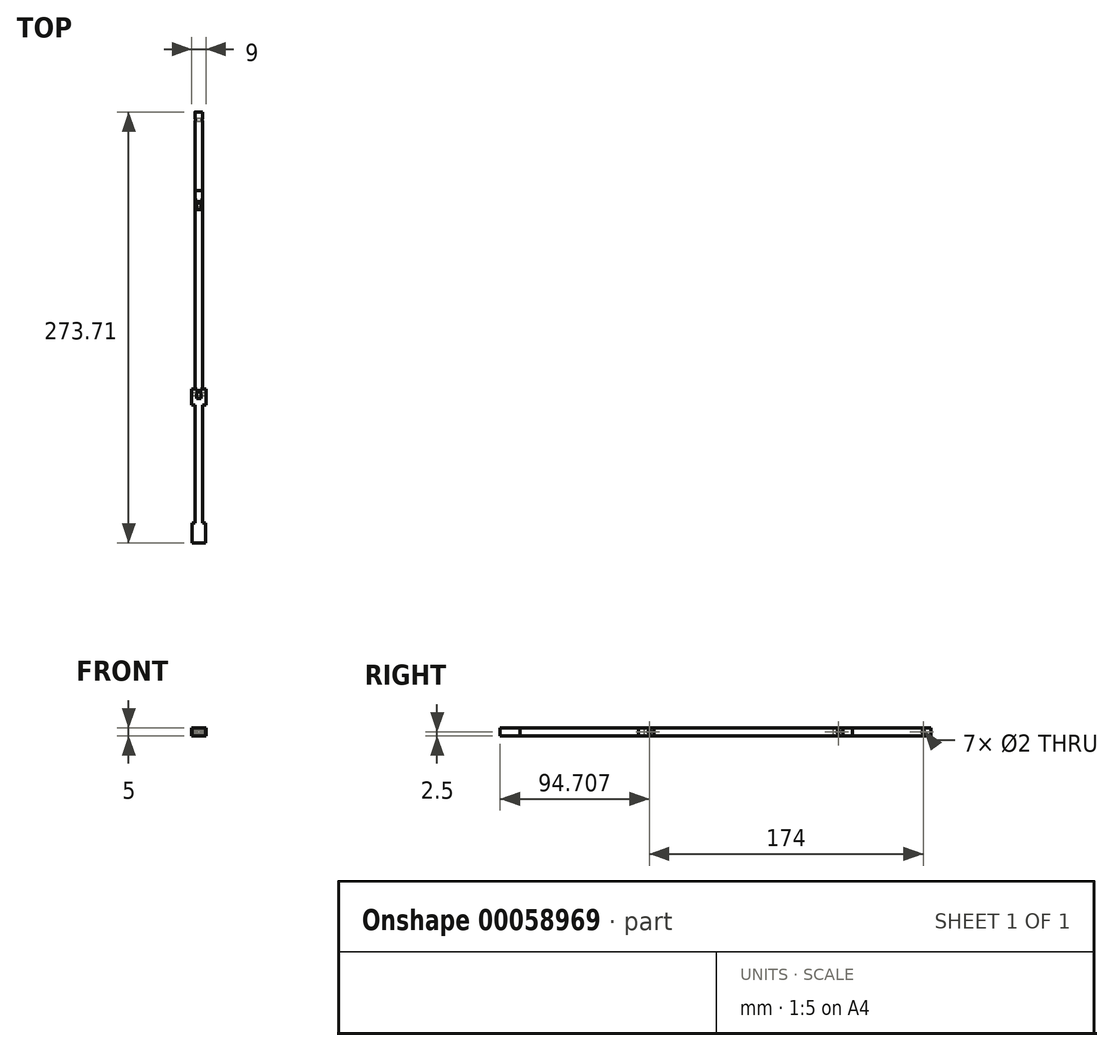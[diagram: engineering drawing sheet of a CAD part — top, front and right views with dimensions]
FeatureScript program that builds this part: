
annotation { "Feature Type Name" : "Feature", "Feature Type Description" : "" }
export const myFeature = defineFeature(function(context is Context, id is Id, definition is map)
    precondition{}
    {
        {
            var Q0;
            Q0=qCreatedBy(makeId("Top.planeOp"),FACE);
            var sketch = newSketch(context, id + "F0", { "sketchPlane" : qUnion([Q0])});
            skLineSegment(sketch, "E0.top", {"start": v(2.38, 39.03) * mm, "end": v(-6.5, 39.03) * mm});
            skLineSegment(sketch, "E0.left", {"start": v(2.38, 26.32) * mm, "end": v(2.38, 39.03) * mm});
            skLineSegment(sketch, "E0.right", {"start": v(-6.5, 26.32) * mm, "end": v(-6.5, 39.03) * mm});
            skLineSegment(sketch, "E1", {"start": v(-6.5, 26.32) * mm, "end": v(2.38, 26.32) * mm});
            skSolve(sketch);
        }
        {
            var Q0;
            Q0=qSketchRegion(id+"F0",true);
            extrude(context, id + "F1", {"entities" : qUnion([Q0]), "depth" : 5 * mm});
        }
        {
            var Q0;
            Q0=makeQuery(id+"F1.opExtrude","SWEPT_FACE",FACE,{"disambiguationData":[OSD([sQuery(id+"F0.wireOp",EDGE,"E0.top")])]});
            var sketch = newSketch(context, id + "F2", { "sketchPlane" : qUnion([Q0])});
            skLineSegment(sketch, "E2.bottom", {"start": v(-2.38, 5) * mm, "end": v(6.5, 5) * mm, "construction": true});
            skLineSegment(sketch, "E2.top", {"start": v(-2.38, 0) * mm, "end": v(6.5, 0) * mm, "construction": true});
            skLineSegment(sketch, "E2.left", {"start": v(-2.38, 5) * mm, "end": v(-2.38, 0) * mm, "construction": true});
            skLineSegment(sketch, "E2.right", {"start": v(6.5, 5) * mm, "end": v(6.5, 0) * mm, "construction": true});
            skLineSegment(sketch, "E3", {"start": v(2.06, 5) * mm, "end": v(2.06, 0) * mm, "construction": true});
            skPoint(sketch, "E4", {"position": v(2.06, 2.5) * mm});
            skLineSegment(sketch, "E5.bottom", {"start": v(-0.44, 5) * mm, "end": v(4.56, 5) * mm});
            skLineSegment(sketch, "E5.top", {"start": v(-0.44, 0) * mm, "end": v(4.56, 0) * mm});
            skLineSegment(sketch, "E5.left", {"start": v(-0.44, 5) * mm, "end": v(-0.44, 0) * mm});
            skLineSegment(sketch, "E5.right", {"start": v(4.56, 5) * mm, "end": v(4.56, 0) * mm});
            skPoint(sketch, "E6", {"position": v(2.06, 5) * mm});
            skSolve(sketch);
        }
        {
            var Q0;
            Q0=makeQuery(id+"F2.imprint","IMPRINT",FACE,{"disambiguationData":[TD([[makeQuery(id+"F2.imprint","IMPRINT",EDGE,{"derivedFrom":sQuery(id+"F2.wireOp",EDGE,"E5.bottom")}),-1.0]])]});
            extrude(context, id + "F3", {"entities" : qUnion([Q0]), "operationType" : NewBodyOperationType.ADD, "depth" : 85 * mm});
        }
        {
            var Q0;
            Q0=makeQuery(id+"F3.boolean.opBoolean","MERGE",FACE,{"derivedFrom":[makeQuery(id+"F1.opExtrude","CAP_FACE",FACE,{"disambiguationData":[OSD([sQuery(id+"F0.wireOp",EDGE,"d9f391bc-674f-497b-be90-560cbfe84b75"),sQuery(id+"F0.wireOp",EDGE,"66b45562-6a73-478d-960d-9298d4f6f7f0"),sQuery(id+"F0.wireOp",EDGE,"14187485-9066-4405-92d3-fc27601e42af"),sQuery(id+"F0.wireOp",EDGE,"531d857a-c366-4fd6-946f-2a201ec59503"),sQuery(id+"F0.wireOp",EDGE,"82b77f9d-e961-41ac-b487-f27284012814"),sQuery(id+"F0.wireOp",EDGE,"7834417a-5e7c-45c5-8e6f-19fbc39ef538"),sQuery(id+"F0.wireOp",EDGE,"300af05a-1d2d-4a39-b159-b80513d7f740"),sQuery(id+"F0.wireOp",EDGE,"1d5f7e8b-d76f-446f-8b3e-2a2f550bd8e3"),sQuery(id+"F0.wireOp",EDGE,"35e8518a-73fa-4b07-8810-64eb534e7b1e"),sQuery(id+"F0.wireOp",EDGE,"18614789-dbbf-47a7-80e0-906205be91d2"),sQuery(id+"F0.wireOp",EDGE,"b77e8b2d-b58d-4b65-9e12-d4334338aa4c"),sQuery(id+"F0.wireOp",EDGE,"9d96ad04-3b06-4638-bbb7-3f0403701198"),sQuery(id+"F0.wireOp",EDGE,"e2f941ec-7ca7-4e10-9b82-3674a8dee568"),sQuery(id+"F0.wireOp",EDGE,"623cfd6c-6096-4034-a234-787e3acb7919"),sQuery(id+"F0.wireOp",EDGE,"effc0b7c-bb45-4b4c-82cf-5a194e7747a9"),sQuery(id+"F0.wireOp",EDGE,"20afc2aa-4987-4b9c-837f-1a90a823d70c"),sQuery(id+"F0.wireOp",EDGE,"93c108a5-420a-46d6-a4f1-9fc166012f6e"),sQuery(id+"F0.wireOp",EDGE,"24f54e41-abe2-49ed-aca4-37dbfc811c90"),sQuery(id+"F0.wireOp",EDGE,"9775e243-409f-4585-bc05-4883512e3564"),sQuery(id+"F0.wireOp",EDGE,"a5e87a16-9f3d-4e96-afb7-1f3010025381"),sQuery(id+"F0.wireOp",EDGE,"57da4376-ad28-41da-a036-1c08f5a0e9fe"),sQuery(id+"F0.wireOp",EDGE,"42ac5c60-1a59-4eb0-a50e-105db2941719"),sQuery(id+"F0.wireOp",EDGE,"7f869c91-c514-4a78-955d-8fa2f71ec013"),sQuery(id+"F0.wireOp",EDGE,"92df5dc1-1633-40e4-82dc-26b14e9fc4fe"),sQuery(id+"F0.wireOp",EDGE,"9fb6344f-8160-4d43-a8ca-7dc5bcb63cf4"),sQuery(id+"F0.wireOp",EDGE,"403433ed-74ab-49ef-b5f3-8321a2a46bc0"),sQuery(id+"F0.wireOp",EDGE,"38791a52-10f3-4032-89cb-9997d4a285ff"),sQuery(id+"F0.wireOp",EDGE,"17827bc5-de02-4b8f-ae35-e25ffe9a3a56"),sQuery(id+"F0.wireOp",EDGE,"ebb8a741-28c9-44e3-8d01-7b9906950363"),sQuery(id+"F0.wireOp",EDGE,"24247562-824f-4080-b562-a07a46203f45"),sQuery(id+"F0.wireOp",EDGE,"61158206-3902-44f4-b84a-59a3b62cea53"),sQuery(id+"F0.wireOp",EDGE,"222b9068-06c2-468c-a816-7dcc0e9861e7"),sQuery(id+"F0.wireOp",EDGE,"1443c47e-cb78-4972-aa1d-b2a5593cacaa"),sQuery(id+"F0.wireOp",EDGE,"4ee5fa2a-e4b7-4507-9879-d4257c452374"),sQuery(id+"F0.wireOp",EDGE,"ac129c3d-c943-4e23-b628-d4f0035e9390"),sQuery(id+"F0.wireOp",EDGE,"a4b60933-6dc5-485c-afad-bad217473213"),sQuery(id+"F0.wireOp",EDGE,"c784899e-bd4b-4296-9021-59274ccaadd9"),sQuery(id+"F0.wireOp",EDGE,"748fc19f-7cd7-4142-921c-8b19d610d3d1"),sQuery(id+"F0.wireOp",EDGE,"ebea3f07-4c38-41c4-ac2c-bac9cb8d1528"),sQuery(id+"F0.wireOp",EDGE,"c6bc3915-ea64-408b-b0c0-442b260292ac"),sQuery(id+"F0.wireOp",EDGE,"15593884-b140-4daf-bfd8-0ecfa5efcbbd"),sQuery(id+"F0.wireOp",EDGE,"a7df4056-7cd6-44bf-9033-605bc9c32d03"),sQuery(id+"F0.wireOp",EDGE,"39d318a8-1c2b-49b4-b444-523ba4d5fcf2"),sQuery(id+"F0.wireOp",EDGE,"11df0492-6635-41a9-8511-0c760388fa34"),sQuery(id+"F0.wireOp",EDGE,"a12d8f92-446a-4b34-a2f5-26c26993d257"),sQuery(id+"F0.wireOp",EDGE,"78a7d225-68f4-4e83-b71e-32c50f125e93"),sQuery(id+"F0.wireOp",EDGE,"1862a963-57d5-471d-8109-9f73d1aa8848"),sQuery(id+"F0.wireOp",EDGE,"54f45445-f8d1-4aff-bece-9da66ad386cd"),sQuery(id+"F0.wireOp",EDGE,"5ba05bdf-983b-4f68-941c-4bf50adfb3c5"),sQuery(id+"F0.wireOp",EDGE,"973eaeb2-d25f-40eb-b74f-e363d637089d"),sQuery(id+"F0.wireOp",EDGE,"9fe65cb9-7a78-4622-86d1-7f23de040810"),sQuery(id+"F0.wireOp",EDGE,"3fe47919-788c-4396-b5fd-8990ec275c22"),sQuery(id+"F0.wireOp",EDGE,"55bf8aa7-cfd1-4645-9e83-de087904feb2"),sQuery(id+"F0.wireOp",EDGE,"c2af9e0f-cc3a-474c-a54e-54ce149af3bb"),sQuery(id+"F0.wireOp",EDGE,"ff518af7-eed7-424f-ad46-c5242196626b"),sQuery(id+"F0.wireOp",EDGE,"cc0332f5-aef5-4de5-a14e-8dcbe21eca6c"),sQuery(id+"F0.wireOp",EDGE,"c5d08f8f-8ed2-45eb-9a75-cb5f251a4d6d"),sQuery(id+"F0.wireOp",EDGE,"5995e242-d37b-4450-9f63-962c7eb38085"),sQuery(id+"F0.wireOp",EDGE,"25f3b115-5ae4-4790-92e5-62a7bc3f5c29"),sQuery(id+"F0.wireOp",EDGE,"2d611a70-a2f5-475a-a6a8-adddd76473ce"),sQuery(id+"F0.wireOp",EDGE,"273bf26d-3f66-4ef4-bf64-d22a533f903a"),sQuery(id+"F0.wireOp",EDGE,"de5f23e0-e1a0-4e15-900e-688ab9168dcd"),sQuery(id+"F0.wireOp",EDGE,"4de6b542-ff3a-44f7-b58e-1e4f3b2cccf4"),sQuery(id+"F0.wireOp",EDGE,"be1b36f0-e020-4af0-baec-c4481b6b9122"),sQuery(id+"F0.wireOp",EDGE,"d7c1d08a-2f0c-4649-94c4-8f89162c768a"),sQuery(id+"F0.wireOp",EDGE,"bd09b6b8-9bc9-4c5b-ab2b-4ede4d9b9cae"),sQuery(id+"F0.wireOp",EDGE,"05b5a1f0-0223-4439-ac6f-cac7d6a05357"),sQuery(id+"F0.wireOp",EDGE,"318e3676-c449-41e0-b4da-e74d07fc2b12"),sQuery(id+"F0.wireOp",EDGE,"31725f89-0695-4483-9200-5756053d80e4"),sQuery(id+"F0.wireOp",EDGE,"e3cb0712-5583-40de-9f57-2bae5fcde790"),sQuery(id+"F0.wireOp",EDGE,"c6456fea-21fc-4931-a427-a856d1f6ee5c"),sQuery(id+"F0.wireOp",EDGE,"e7d8b0b0-a421-4050-b770-ef5136dc3e4d"),sQuery(id+"F0.wireOp",EDGE,"0788d0b0-f754-45d8-aefc-a91755a03ac1"),sQuery(id+"F0.wireOp",EDGE,"fc27efed-591c-43cc-b4b2-6872e1742544"),sQuery(id+"F0.wireOp",EDGE,"82c2f9b8-58bc-4a33-9bd5-fec435af3e72"),sQuery(id+"F0.wireOp",EDGE,"2e300663-fb6b-4f29-9ebf-a9fab34af9c4"),sQuery(id+"F0.wireOp",EDGE,"3d2dfd07-a0b9-43b8-893f-685d0a355372"),sQuery(id+"F0.wireOp",EDGE,"e776ef69-6530-4f3d-8924-f9840dcd9e4d"),sQuery(id+"F0.wireOp",EDGE,"6dcbcc22-e493-4400-9b8a-7eed73031bc4"),sQuery(id+"F0.wireOp",EDGE,"7cdd9895-84d3-47ea-86bd-688608d79eca"),sQuery(id+"F0.wireOp",EDGE,"3a7bfdfd-3144-4dae-8888-a8bcf2221552"),sQuery(id+"F0.wireOp",EDGE,"2953d7e0-23a1-472e-bf8c-49982d9a56d6"),sQuery(id+"F0.wireOp",EDGE,"846718aa-0a8a-476e-8a52-f2d355658347"),sQuery(id+"F0.wireOp",EDGE,"13e02fad-2dbd-4394-a12b-883b621fb0cf"),sQuery(id+"F0.wireOp",EDGE,"9bfc4f6e-5194-4c80-9375-02c13d7037c7"),sQuery(id+"F0.wireOp",EDGE,"4cc90906-b22a-4bfe-9933-4a2b42c67043"),sQuery(id+"F0.wireOp",EDGE,"c3968d64-93bc-4dc6-b8a7-840e206f0e92"),sQuery(id+"F0.wireOp",EDGE,"cff9c3c0-4237-426c-aea8-7115d6da3525"),sQuery(id+"F0.wireOp",EDGE,"76e5b534-b14d-4a45-9111-d87c94f3d3da"),sQuery(id+"F0.wireOp",EDGE,"96eb4b59-6d18-41e9-8181-93777d457c04"),sQuery(id+"F0.wireOp",EDGE,"4b80822d-625d-4929-946d-bb2fee906de1"),sQuery(id+"F0.wireOp",EDGE,"a1b1815c-0f60-4723-aacc-aafe0ccbf065"),sQuery(id+"F0.wireOp",EDGE,"63631a9c-c3d0-4e34-b42e-cf718a2aa654"),sQuery(id+"F0.wireOp",EDGE,"291662e0-8a9a-4794-9b05-15f69232fded"),sQuery(id+"F0.wireOp",EDGE,"c31bbd6a-e51d-4bda-bb55-a930242c1aae"),sQuery(id+"F0.wireOp",EDGE,"6cc65a5c-01cd-414d-b4bf-16365d086d8b"),sQuery(id+"F0.wireOp",EDGE,"0f6044bc-5aed-4332-8dd0-ed4f837cf9c8"),sQuery(id+"F0.wireOp",EDGE,"68f51909-fb33-4c21-8354-d3ee43222832"),sQuery(id+"F0.wireOp",EDGE,"0ba4c335-165f-4c3e-a523-b257962ab2b9"),sQuery(id+"F0.wireOp",EDGE,"a8ab603d-6f8c-4c2b-bc3e-a90f3d25e983"),sQuery(id+"F0.wireOp",EDGE,"3346a9eb-c449-4294-82ff-d0765618b8c3"),sQuery(id+"F0.wireOp",EDGE,"efd91459-38fa-452e-891e-edab332f6489"),sQuery(id+"F0.wireOp",EDGE,"85b94afd-6a00-47ab-a374-eb0a6b957af6"),sQuery(id+"F0.wireOp",EDGE,"71bbe033-8d0c-4649-8752-095e423e4446"),sQuery(id+"F0.wireOp",EDGE,"313f4505-8deb-44f7-a07b-deab9fdd4fca"),sQuery(id+"F0.wireOp",EDGE,"58514e34-5bb3-46cf-af5d-05d66b0c10f9"),sQuery(id+"F0.wireOp",EDGE,"9c61e8f2-2ab1-4688-a9d6-5c20a88d6f6a"),sQuery(id+"F0.wireOp",EDGE,"f84fcc24-327f-4d24-8afc-1352f07d6813"),sQuery(id+"F0.wireOp",EDGE,"2217ef4b-fa2d-4c42-8d86-ed7db710f5bd"),sQuery(id+"F0.wireOp",EDGE,"d87f30a8-b645-4562-81e4-3c3cf9cd6438"),sQuery(id+"F0.wireOp",EDGE,"6b1cc9ff-038e-4fc2-952b-8fefe25711b2"),sQuery(id+"F0.wireOp",EDGE,"9b0d0940-50e4-4c60-959e-8cb1c47cda3d"),sQuery(id+"F0.wireOp",EDGE,"fd67a80c-15d7-4a10-bc2d-74f667f92aae"),sQuery(id+"F0.wireOp",EDGE,"ce9cbc48-37c6-4742-bee7-228e45a917e3"),sQuery(id+"F0.wireOp",EDGE,"668236f6-3d49-4ccf-890f-7b693b95a113"),sQuery(id+"F0.wireOp",EDGE,"f978c870-af19-49dc-a3f6-58e714ba6b8d"),sQuery(id+"F0.wireOp",EDGE,"3c9fd5d7-5c91-4e2a-8e90-77909dfb583b"),sQuery(id+"F0.wireOp",EDGE,"3f653433-d41a-442d-9af1-f4ba11755801"),sQuery(id+"F0.wireOp",EDGE,"3e1bc7f2-4028-408e-8046-60d3c4eab3db"),sQuery(id+"F0.wireOp",EDGE,"6e5cb531-4b2f-424d-b6a2-fd274bbfcedc"),sQuery(id+"F0.wireOp",EDGE,"47450d10-22bf-4260-9408-7e53fd283f2d"),sQuery(id+"F0.wireOp",EDGE,"6d45c327-3d4d-4948-b28d-f57c85b01b79"),sQuery(id+"F0.wireOp",EDGE,"09a427cb-33ca-4fdc-b261-2336e21235b2"),sQuery(id+"F0.wireOp",EDGE,"518944ec-1655-4f40-b183-544c6dabeccc"),sQuery(id+"F0.wireOp",EDGE,"9a21c479-1b04-474c-b49a-7bb92b3e97ee"),sQuery(id+"F0.wireOp",EDGE,"96faa4f8-2343-44d0-b0c9-daf9f0cf2026"),sQuery(id+"F0.wireOp",EDGE,"6fc17f55-5333-4b57-a339-275bf10e1425"),sQuery(id+"F0.wireOp",EDGE,"42fdd7f3-cbb8-400e-a0d9-d82489298c17"),sQuery(id+"F0.wireOp",EDGE,"ff3833a1-8283-4137-914b-97420855596c"),sQuery(id+"F0.wireOp",EDGE,"6d86c47c-1e01-4b32-ae2a-396aeb5aa8c3"),sQuery(id+"F0.wireOp",EDGE,"3656029b-9af7-4a6b-91c7-0cb8f82c84b0"),sQuery(id+"F0.wireOp",EDGE,"c5a5c181-3903-47b5-9841-0451d0b8c190"),sQuery(id+"F0.wireOp",EDGE,"6b476b77-b2de-421b-b26d-88dcbb17dccc"),sQuery(id+"F0.wireOp",EDGE,"3d318069-a1b2-4ca5-910a-b32c13e6ff0f"),sQuery(id+"F0.wireOp",EDGE,"9330180f-a560-47bb-918b-d92eebda0b31"),sQuery(id+"F0.wireOp",EDGE,"b318f770-8e99-4d49-b667-ae16576ab8c5"),sQuery(id+"F0.wireOp",EDGE,"e8c7022b-339d-4a50-8e2c-c0ad6522d806"),sQuery(id+"F0.wireOp",EDGE,"e86b4955-e698-4ab7-84b9-7f9632085e45"),sQuery(id+"F0.wireOp",EDGE,"0c38cf30-4431-4dda-a171-e1c8e016ea24"),sQuery(id+"F0.wireOp",EDGE,"f094b2ba-6a66-4d13-8490-6bb0ce785aa8"),sQuery(id+"F0.wireOp",EDGE,"41e1ebd6-8c90-401f-a72a-f212800231e3"),sQuery(id+"F0.wireOp",EDGE,"40e70cb6-71ec-4d67-b914-e8ee82708b93"),sQuery(id+"F0.wireOp",EDGE,"13f06e0a-f10b-47e7-959c-6b309f65aed5"),sQuery(id+"F0.wireOp",EDGE,"3fa473f8-a0ea-440b-8ccf-443d736f73d8"),sQuery(id+"F0.wireOp",EDGE,"3ff53a63-1f71-4b9e-b5b1-fe861864c7b9"),sQuery(id+"F0.wireOp",EDGE,"9fd11a8c-801f-433b-8a68-149d040764ea"),sQuery(id+"F0.wireOp",EDGE,"2b57bb01-2787-4d2a-a1f7-a8f2ac708940"),sQuery(id+"F0.wireOp",EDGE,"b3a649f2-00b2-4941-a5f4-54f2790e47c9"),sQuery(id+"F0.wireOp",EDGE,"689af078-1fc4-4801-82f7-c259a968d8e3"),sQuery(id+"F0.wireOp",EDGE,"4afb566c-1766-4da3-aeca-2e561b661cbf"),sQuery(id+"F0.wireOp",EDGE,"afbdcd0b-9ccb-41a6-b5df-fe1bcf30544d"),sQuery(id+"F0.wireOp",EDGE,"0a1a2607-09d2-45da-b494-66f0f4572d53"),sQuery(id+"F0.wireOp",EDGE,"df9dc95f-9734-4203-a4b0-b50527c86d60"),sQuery(id+"F0.wireOp",EDGE,"868db6a5-4ab0-468d-816c-25f0bc18b053"),sQuery(id+"F0.wireOp",EDGE,"aaa1c0b5-afc6-4e25-82a0-d6f0aaf8ec45"),sQuery(id+"F0.wireOp",EDGE,"450ffb83-aa88-433e-99e9-7fc4bc443133"),sQuery(id+"F0.wireOp",EDGE,"7c9dc92b-bdbd-4c2f-ba2f-b681be311a02"),sQuery(id+"F0.wireOp",EDGE,"d8d805bb-8432-4448-99fe-12ddf517f87f"),sQuery(id+"F0.wireOp",EDGE,"e1c897c1-2833-4eab-81cd-6ccc64de02e8"),sQuery(id+"F0.wireOp",EDGE,"12eef9dd-bb38-451e-8b46-68758d02cc0e"),sQuery(id+"F0.wireOp",EDGE,"f6b90299-a189-4960-beb2-75c4f087d852"),sQuery(id+"F0.wireOp",EDGE,"d44cce74-31fd-4baf-a4a6-ccbb4521b524"),sQuery(id+"F0.wireOp",EDGE,"26311da7-8aed-42c2-aa0d-06719439663e"),sQuery(id+"F0.wireOp",EDGE,"bfe2dd46-ca33-42a6-b3e5-4bcb679aff27"),sQuery(id+"F0.wireOp",EDGE,"f7121924-5964-4ee7-8e7a-9366b6055faf"),sQuery(id+"F0.wireOp",EDGE,"baddc95a-3768-4696-a9fc-c3c93e777550"),sQuery(id+"F0.wireOp",EDGE,"4cbcd0b8-8d3f-4500-b314-949e4192bba6"),sQuery(id+"F0.wireOp",EDGE,"573feae8-dbb2-4ee3-84b1-a2f0e784b4ce"),sQuery(id+"F0.wireOp",EDGE,"1491502b-4fac-4339-bddb-72d872b244a9"),sQuery(id+"F0.wireOp",EDGE,"ed8966f0-f9a2-415f-b3ef-00e8bec5a987"),sQuery(id+"F0.wireOp",EDGE,"42659012-de86-4715-a0b8-c198bc09b6c3"),sQuery(id+"F0.wireOp",EDGE,"eba869ca-ba70-4ef3-90af-459470689084"),sQuery(id+"F0.wireOp",EDGE,"9875f08d-c713-4704-93cd-788487ec0e6b"),sQuery(id+"F0.wireOp",EDGE,"88c7c1a6-46c1-45f7-a284-4e760e0ff227"),sQuery(id+"F0.wireOp",EDGE,"7296298e-4422-4531-89ec-245f94a1b7ce"),sQuery(id+"F0.wireOp",EDGE,"d982fd75-f615-4661-88e5-4d338e35f5d6"),sQuery(id+"F0.wireOp",EDGE,"855cb7c2-4006-4b69-ae1d-061ed893761e"),sQuery(id+"F0.wireOp",EDGE,"25f14cae-63dd-43dd-a2cf-069ce091aab3"),sQuery(id+"F0.wireOp",EDGE,"8dd2c990-ce8b-4ae6-88a5-6f7d81b76fb7"),sQuery(id+"F0.wireOp",EDGE,"50c487b6-7ae5-43ad-9b89-c44e1cfbe420"),sQuery(id+"F0.wireOp",EDGE,"28defd30-3f37-4457-b5ce-98c8ab6f0938"),sQuery(id+"F0.wireOp",EDGE,"25b26be1-608d-4fca-8147-ce63c78e7ef9"),sQuery(id+"F0.wireOp",EDGE,"55286520-3f9c-4cb0-8993-b41f90c1e7b2"),sQuery(id+"F0.wireOp",EDGE,"8b04d12e-496a-4f5a-9f87-f93561172584"),sQuery(id+"F0.wireOp",EDGE,"69f61a6b-229e-4c46-8902-5dacc0b3caa7"),sQuery(id+"F0.wireOp",EDGE,"b70ecf2a-3e9d-42b0-a09c-c895f72a43f5"),sQuery(id+"F0.wireOp",EDGE,"b4318e1e-f674-42cb-b4b4-c6a7f0d1058b"),sQuery(id+"F0.wireOp",EDGE,"0a5737aa-f65d-4c08-8fa3-74cd1c6bc787"),sQuery(id+"F0.wireOp",EDGE,"2b114e95-5b76-41c0-af98-aa6b4118be67"),sQuery(id+"F0.wireOp",EDGE,"909ff558-2fcb-4b4a-b58c-44165d3143ec"),sQuery(id+"F0.wireOp",EDGE,"03647ff9-6972-4830-a77b-507609320f8a"),sQuery(id+"F0.wireOp",EDGE,"784304f5-69fc-4c5d-a15a-a01099708ad1"),sQuery(id+"F0.wireOp",EDGE,"7e862998-cb3b-43fa-98f0-afa86e38354f"),sQuery(id+"F0.wireOp",EDGE,"b133dd31-da7f-4d34-b041-a02e12d47f77"),sQuery(id+"F0.wireOp",EDGE,"c20fe978-2982-45a4-865c-b8fa9effb66d"),sQuery(id+"F0.wireOp",EDGE,"ecc07ede-e418-4cc6-ac17-b0618c730539"),sQuery(id+"F0.wireOp",EDGE,"a72532f4-d06f-446a-a491-5e0e52dccc34"),sQuery(id+"F0.wireOp",EDGE,"e80db44c-f0a2-44c0-9d9a-ac9ec1fdb025"),sQuery(id+"F0.wireOp",EDGE,"a256cc86-e2ce-4537-87d8-996e6a32e2c3"),sQuery(id+"F0.wireOp",EDGE,"9d600fab-17dd-4d7f-9bf9-2e90aad73a65"),sQuery(id+"F0.wireOp",EDGE,"5042385b-9870-4c5e-be6a-0c3db3c46120"),sQuery(id+"F0.wireOp",EDGE,"31a5a34f-51f7-4c3e-8b64-8b1dabd0146e"),sQuery(id+"F0.wireOp",EDGE,"6b2aa247-f6cb-4ed4-b715-b1f137de6caf"),sQuery(id+"F0.wireOp",EDGE,"66b72c40-0d5e-4a0b-9279-31ab5fa1e7fe"),sQuery(id+"F0.wireOp",EDGE,"15e6370f-fd6b-4262-9e07-4cd19af6e575"),sQuery(id+"F0.wireOp",EDGE,"42ae2dfc-64aa-47e2-8300-2f233e3b2cdc"),sQuery(id+"F0.wireOp",EDGE,"f1330061-7111-4682-b376-6b8410619920"),sQuery(id+"F0.wireOp",EDGE,"4f299f36-5b62-45e5-935a-49dea53b4436"),sQuery(id+"F0.wireOp",EDGE,"f4a1d07d-759c-4b8c-a361-16f86e8a581b"),sQuery(id+"F0.wireOp",EDGE,"a197af79-e1d5-4cc2-bcad-7eec1b0bb374"),sQuery(id+"F0.wireOp",EDGE,"0b645705-9a78-41e4-bf43-11811c5310d6"),sQuery(id+"F0.wireOp",EDGE,"3b8b7332-f98f-4427-9e20-b42ec5fb5940"),sQuery(id+"F0.wireOp",EDGE,"dac7c135-5026-46cf-917a-981712ef2904"),sQuery(id+"F0.wireOp",EDGE,"e792f283-39e8-4103-9782-e05d206dbdd8"),sQuery(id+"F0.wireOp",EDGE,"c4719064-44fe-4252-b3a6-de5fb7a830d2"),sQuery(id+"F0.wireOp",EDGE,"0bf6103d-bcda-4bbf-96c7-54e6ef03cde9"),sQuery(id+"F0.wireOp",EDGE,"e9d37db2-ae33-474e-9755-d6a2f55bc904"),sQuery(id+"F0.wireOp",EDGE,"E0.top"),sQuery(id+"F0.wireOp",EDGE,"E0.left"),sQuery(id+"F0.wireOp",EDGE,"E0.right")])],"isStart":false}),makeQuery(id+"F3.opExtrude","SWEPT_FACE",FACE,{"disambiguationData":[OSD([sQuery(id+"F2.wireOp",EDGE,"E5.bottom")])]})]});
            var sketch = newSketch(context, id + "F4", { "sketchPlane" : qUnion([Q0])});
            skLineSegment(sketch, "E7.bottom", {"start": v(-4.56, 124.03) * mm, "end": v(0.44, 124.03) * mm, "construction": true});
            skLineSegment(sketch, "E7.top", {"start": v(-4.56, 114.03) * mm, "end": v(0.44, 114.03) * mm, "construction": true});
            skLineSegment(sketch, "E7.left", {"start": v(-4.56, 124.03) * mm, "end": v(-4.56, 114.03) * mm, "construction": true});
            skLineSegment(sketch, "E7.right", {"start": v(0.44, 124.03) * mm, "end": v(0.44, 114.03) * mm, "construction": true});
            skPoint(sketch, "E8", {"position": v(-2.06, 124.03) * mm});
            skLineSegment(sketch, "E9", {"start": v(-2.06, 124.03) * mm, "end": v(-2.06, 118.03) * mm, "construction": true});
            skLineSegment(sketch, "E10", {"start": v(-3.06, 124.03) * mm, "end": v(-1.06, 124.03) * mm});
            skLineSegment(sketch, "E11", {"start": v(-3.56, 118.03) * mm, "end": v(-0.56, 118.03) * mm});
            skPoint(sketch, "E12", {"position": v(-2.06, 118.03) * mm});
            skLineSegment(sketch, "E13", {"start": v(-3.06, 124.03) * mm, "end": v(-3.56, 118.03) * mm});
            skLineSegment(sketch, "E14", {"start": v(-1.06, 124.03) * mm, "end": v(-0.56, 118.03) * mm});
            skLineSegment(sketch, "E15.bottom", {"start": v(-6.56, 124.03) * mm, "end": v(2.44, 124.03) * mm});
            skLineSegment(sketch, "E15.top", {"start": v(-6.56, 114.03) * mm, "end": v(2.44, 114.03) * mm});
            skLineSegment(sketch, "E15.left", {"start": v(-6.56, 124.03) * mm, "end": v(-6.56, 114.03) * mm});
            skLineSegment(sketch, "E15.right", {"start": v(2.44, 124.03) * mm, "end": v(2.44, 114.03) * mm});
            skSolve(sketch);
        }
        {
            var Q0;
            {var subQ3=sQuery(id+"F4.wireOp",EDGE,"E15.left");Q0=makeQuery(id+"F4.imprint","IMPRINT",FACE,{"disambiguationData":[TD([[makeQuery(id+"F4.imprint","IMPRINT",EDGE,{"derivedFrom":subQ3}),1.0]])]});}
            var Q1;
            {var subQ3=sQuery(id+"F4.wireOp",EDGE,"E15.right");Q1=makeQuery(id+"F4.imprint","IMPRINT",FACE,{"disambiguationData":[TD([[makeQuery(id+"F4.imprint","IMPRINT",EDGE,{"derivedFrom":subQ3}),-1.0]])]});}
            extrude(context, id + "F5", {"entities" : qUnion([Q0, Q1]), "operationType" : NewBodyOperationType.ADD, "oppositeDirection" : true, "depth" : 5 * mm});
        }
        {
            var Q0;
            Q0=makeQuery(id+"F4.imprint","IMPRINT",FACE,{"disambiguationData":[TD([[makeQuery(id+"F4.imprint","IMPRINT",EDGE,{"derivedFrom":sQuery(id+"F4.wireOp",EDGE,"E11")}),1.0]])]});
            extrude(context, id + "F6", {"entities" : qUnion([Q0]), "operationType" : NewBodyOperationType.REMOVE, "oppositeDirection" : true, "depth" : 5 * mm});
        }
        {
            var Q0;
            {var subQ0=sQuery(id+"F4.wireOp",EDGE,"E15.top");var subQ1=sQuery(id+"F4.wireOp",EDGE,"E15.bottom");var subQ2=sQuery(id+"F2.wireOp",EDGE,"E5.bottom");var subQ3=sQuery(id+"F0.wireOp",EDGE,"E0.top");Q0=makeQuery(id+"F5.boolean.opBoolean","MERGE",FACE,{"derivedFrom":[makeQuery(id+"F3.boolean.opBoolean","MERGE",FACE,{"derivedFrom":[makeQuery(id+"F1.opExtrude","CAP_FACE",FACE,{"disambiguationData":[OSD([sQuery(id+"F0.wireOp",EDGE,"d9f391bc-674f-497b-be90-560cbfe84b75"),sQuery(id+"F0.wireOp",EDGE,"66b45562-6a73-478d-960d-9298d4f6f7f0"),sQuery(id+"F0.wireOp",EDGE,"14187485-9066-4405-92d3-fc27601e42af"),sQuery(id+"F0.wireOp",EDGE,"531d857a-c366-4fd6-946f-2a201ec59503"),sQuery(id+"F0.wireOp",EDGE,"82b77f9d-e961-41ac-b487-f27284012814"),sQuery(id+"F0.wireOp",EDGE,"7834417a-5e7c-45c5-8e6f-19fbc39ef538"),sQuery(id+"F0.wireOp",EDGE,"300af05a-1d2d-4a39-b159-b80513d7f740"),sQuery(id+"F0.wireOp",EDGE,"1d5f7e8b-d76f-446f-8b3e-2a2f550bd8e3"),sQuery(id+"F0.wireOp",EDGE,"35e8518a-73fa-4b07-8810-64eb534e7b1e"),sQuery(id+"F0.wireOp",EDGE,"18614789-dbbf-47a7-80e0-906205be91d2"),sQuery(id+"F0.wireOp",EDGE,"b77e8b2d-b58d-4b65-9e12-d4334338aa4c"),sQuery(id+"F0.wireOp",EDGE,"9d96ad04-3b06-4638-bbb7-3f0403701198"),sQuery(id+"F0.wireOp",EDGE,"e2f941ec-7ca7-4e10-9b82-3674a8dee568"),sQuery(id+"F0.wireOp",EDGE,"623cfd6c-6096-4034-a234-787e3acb7919"),sQuery(id+"F0.wireOp",EDGE,"effc0b7c-bb45-4b4c-82cf-5a194e7747a9"),sQuery(id+"F0.wireOp",EDGE,"20afc2aa-4987-4b9c-837f-1a90a823d70c"),sQuery(id+"F0.wireOp",EDGE,"93c108a5-420a-46d6-a4f1-9fc166012f6e"),sQuery(id+"F0.wireOp",EDGE,"24f54e41-abe2-49ed-aca4-37dbfc811c90"),sQuery(id+"F0.wireOp",EDGE,"9775e243-409f-4585-bc05-4883512e3564"),sQuery(id+"F0.wireOp",EDGE,"a5e87a16-9f3d-4e96-afb7-1f3010025381"),sQuery(id+"F0.wireOp",EDGE,"57da4376-ad28-41da-a036-1c08f5a0e9fe"),sQuery(id+"F0.wireOp",EDGE,"42ac5c60-1a59-4eb0-a50e-105db2941719"),sQuery(id+"F0.wireOp",EDGE,"7f869c91-c514-4a78-955d-8fa2f71ec013"),sQuery(id+"F0.wireOp",EDGE,"92df5dc1-1633-40e4-82dc-26b14e9fc4fe"),sQuery(id+"F0.wireOp",EDGE,"9fb6344f-8160-4d43-a8ca-7dc5bcb63cf4"),sQuery(id+"F0.wireOp",EDGE,"403433ed-74ab-49ef-b5f3-8321a2a46bc0"),sQuery(id+"F0.wireOp",EDGE,"38791a52-10f3-4032-89cb-9997d4a285ff"),sQuery(id+"F0.wireOp",EDGE,"17827bc5-de02-4b8f-ae35-e25ffe9a3a56"),sQuery(id+"F0.wireOp",EDGE,"ebb8a741-28c9-44e3-8d01-7b9906950363"),sQuery(id+"F0.wireOp",EDGE,"24247562-824f-4080-b562-a07a46203f45"),sQuery(id+"F0.wireOp",EDGE,"61158206-3902-44f4-b84a-59a3b62cea53"),sQuery(id+"F0.wireOp",EDGE,"222b9068-06c2-468c-a816-7dcc0e9861e7"),sQuery(id+"F0.wireOp",EDGE,"1443c47e-cb78-4972-aa1d-b2a5593cacaa"),sQuery(id+"F0.wireOp",EDGE,"4ee5fa2a-e4b7-4507-9879-d4257c452374"),sQuery(id+"F0.wireOp",EDGE,"ac129c3d-c943-4e23-b628-d4f0035e9390"),sQuery(id+"F0.wireOp",EDGE,"a4b60933-6dc5-485c-afad-bad217473213"),sQuery(id+"F0.wireOp",EDGE,"c784899e-bd4b-4296-9021-59274ccaadd9"),sQuery(id+"F0.wireOp",EDGE,"748fc19f-7cd7-4142-921c-8b19d610d3d1"),sQuery(id+"F0.wireOp",EDGE,"ebea3f07-4c38-41c4-ac2c-bac9cb8d1528"),sQuery(id+"F0.wireOp",EDGE,"c6bc3915-ea64-408b-b0c0-442b260292ac"),sQuery(id+"F0.wireOp",EDGE,"15593884-b140-4daf-bfd8-0ecfa5efcbbd"),sQuery(id+"F0.wireOp",EDGE,"a7df4056-7cd6-44bf-9033-605bc9c32d03"),sQuery(id+"F0.wireOp",EDGE,"39d318a8-1c2b-49b4-b444-523ba4d5fcf2"),sQuery(id+"F0.wireOp",EDGE,"11df0492-6635-41a9-8511-0c760388fa34"),sQuery(id+"F0.wireOp",EDGE,"a12d8f92-446a-4b34-a2f5-26c26993d257"),sQuery(id+"F0.wireOp",EDGE,"78a7d225-68f4-4e83-b71e-32c50f125e93"),sQuery(id+"F0.wireOp",EDGE,"1862a963-57d5-471d-8109-9f73d1aa8848"),sQuery(id+"F0.wireOp",EDGE,"54f45445-f8d1-4aff-bece-9da66ad386cd"),sQuery(id+"F0.wireOp",EDGE,"5ba05bdf-983b-4f68-941c-4bf50adfb3c5"),sQuery(id+"F0.wireOp",EDGE,"973eaeb2-d25f-40eb-b74f-e363d637089d"),sQuery(id+"F0.wireOp",EDGE,"9fe65cb9-7a78-4622-86d1-7f23de040810"),sQuery(id+"F0.wireOp",EDGE,"3fe47919-788c-4396-b5fd-8990ec275c22"),sQuery(id+"F0.wireOp",EDGE,"55bf8aa7-cfd1-4645-9e83-de087904feb2"),sQuery(id+"F0.wireOp",EDGE,"c2af9e0f-cc3a-474c-a54e-54ce149af3bb"),sQuery(id+"F0.wireOp",EDGE,"ff518af7-eed7-424f-ad46-c5242196626b"),sQuery(id+"F0.wireOp",EDGE,"cc0332f5-aef5-4de5-a14e-8dcbe21eca6c"),sQuery(id+"F0.wireOp",EDGE,"c5d08f8f-8ed2-45eb-9a75-cb5f251a4d6d"),sQuery(id+"F0.wireOp",EDGE,"5995e242-d37b-4450-9f63-962c7eb38085"),sQuery(id+"F0.wireOp",EDGE,"25f3b115-5ae4-4790-92e5-62a7bc3f5c29"),sQuery(id+"F0.wireOp",EDGE,"2d611a70-a2f5-475a-a6a8-adddd76473ce"),sQuery(id+"F0.wireOp",EDGE,"273bf26d-3f66-4ef4-bf64-d22a533f903a"),sQuery(id+"F0.wireOp",EDGE,"de5f23e0-e1a0-4e15-900e-688ab9168dcd"),sQuery(id+"F0.wireOp",EDGE,"4de6b542-ff3a-44f7-b58e-1e4f3b2cccf4"),sQuery(id+"F0.wireOp",EDGE,"be1b36f0-e020-4af0-baec-c4481b6b9122"),sQuery(id+"F0.wireOp",EDGE,"d7c1d08a-2f0c-4649-94c4-8f89162c768a"),sQuery(id+"F0.wireOp",EDGE,"bd09b6b8-9bc9-4c5b-ab2b-4ede4d9b9cae"),sQuery(id+"F0.wireOp",EDGE,"05b5a1f0-0223-4439-ac6f-cac7d6a05357"),sQuery(id+"F0.wireOp",EDGE,"318e3676-c449-41e0-b4da-e74d07fc2b12"),sQuery(id+"F0.wireOp",EDGE,"31725f89-0695-4483-9200-5756053d80e4"),sQuery(id+"F0.wireOp",EDGE,"e3cb0712-5583-40de-9f57-2bae5fcde790"),sQuery(id+"F0.wireOp",EDGE,"c6456fea-21fc-4931-a427-a856d1f6ee5c"),sQuery(id+"F0.wireOp",EDGE,"e7d8b0b0-a421-4050-b770-ef5136dc3e4d"),sQuery(id+"F0.wireOp",EDGE,"0788d0b0-f754-45d8-aefc-a91755a03ac1"),sQuery(id+"F0.wireOp",EDGE,"fc27efed-591c-43cc-b4b2-6872e1742544"),sQuery(id+"F0.wireOp",EDGE,"82c2f9b8-58bc-4a33-9bd5-fec435af3e72"),sQuery(id+"F0.wireOp",EDGE,"2e300663-fb6b-4f29-9ebf-a9fab34af9c4"),sQuery(id+"F0.wireOp",EDGE,"3d2dfd07-a0b9-43b8-893f-685d0a355372"),sQuery(id+"F0.wireOp",EDGE,"e776ef69-6530-4f3d-8924-f9840dcd9e4d"),sQuery(id+"F0.wireOp",EDGE,"6dcbcc22-e493-4400-9b8a-7eed73031bc4"),sQuery(id+"F0.wireOp",EDGE,"7cdd9895-84d3-47ea-86bd-688608d79eca"),sQuery(id+"F0.wireOp",EDGE,"3a7bfdfd-3144-4dae-8888-a8bcf2221552"),sQuery(id+"F0.wireOp",EDGE,"2953d7e0-23a1-472e-bf8c-49982d9a56d6"),sQuery(id+"F0.wireOp",EDGE,"846718aa-0a8a-476e-8a52-f2d355658347"),sQuery(id+"F0.wireOp",EDGE,"13e02fad-2dbd-4394-a12b-883b621fb0cf"),sQuery(id+"F0.wireOp",EDGE,"9bfc4f6e-5194-4c80-9375-02c13d7037c7"),sQuery(id+"F0.wireOp",EDGE,"4cc90906-b22a-4bfe-9933-4a2b42c67043"),sQuery(id+"F0.wireOp",EDGE,"c3968d64-93bc-4dc6-b8a7-840e206f0e92"),sQuery(id+"F0.wireOp",EDGE,"cff9c3c0-4237-426c-aea8-7115d6da3525"),sQuery(id+"F0.wireOp",EDGE,"76e5b534-b14d-4a45-9111-d87c94f3d3da"),sQuery(id+"F0.wireOp",EDGE,"96eb4b59-6d18-41e9-8181-93777d457c04"),sQuery(id+"F0.wireOp",EDGE,"4b80822d-625d-4929-946d-bb2fee906de1"),sQuery(id+"F0.wireOp",EDGE,"a1b1815c-0f60-4723-aacc-aafe0ccbf065"),sQuery(id+"F0.wireOp",EDGE,"63631a9c-c3d0-4e34-b42e-cf718a2aa654"),sQuery(id+"F0.wireOp",EDGE,"291662e0-8a9a-4794-9b05-15f69232fded"),sQuery(id+"F0.wireOp",EDGE,"c31bbd6a-e51d-4bda-bb55-a930242c1aae"),sQuery(id+"F0.wireOp",EDGE,"6cc65a5c-01cd-414d-b4bf-16365d086d8b"),sQuery(id+"F0.wireOp",EDGE,"0f6044bc-5aed-4332-8dd0-ed4f837cf9c8"),sQuery(id+"F0.wireOp",EDGE,"68f51909-fb33-4c21-8354-d3ee43222832"),sQuery(id+"F0.wireOp",EDGE,"0ba4c335-165f-4c3e-a523-b257962ab2b9"),sQuery(id+"F0.wireOp",EDGE,"a8ab603d-6f8c-4c2b-bc3e-a90f3d25e983"),sQuery(id+"F0.wireOp",EDGE,"3346a9eb-c449-4294-82ff-d0765618b8c3"),sQuery(id+"F0.wireOp",EDGE,"efd91459-38fa-452e-891e-edab332f6489"),sQuery(id+"F0.wireOp",EDGE,"85b94afd-6a00-47ab-a374-eb0a6b957af6"),sQuery(id+"F0.wireOp",EDGE,"71bbe033-8d0c-4649-8752-095e423e4446"),sQuery(id+"F0.wireOp",EDGE,"313f4505-8deb-44f7-a07b-deab9fdd4fca"),sQuery(id+"F0.wireOp",EDGE,"58514e34-5bb3-46cf-af5d-05d66b0c10f9"),sQuery(id+"F0.wireOp",EDGE,"9c61e8f2-2ab1-4688-a9d6-5c20a88d6f6a"),sQuery(id+"F0.wireOp",EDGE,"f84fcc24-327f-4d24-8afc-1352f07d6813"),sQuery(id+"F0.wireOp",EDGE,"2217ef4b-fa2d-4c42-8d86-ed7db710f5bd"),sQuery(id+"F0.wireOp",EDGE,"d87f30a8-b645-4562-81e4-3c3cf9cd6438"),sQuery(id+"F0.wireOp",EDGE,"6b1cc9ff-038e-4fc2-952b-8fefe25711b2"),sQuery(id+"F0.wireOp",EDGE,"9b0d0940-50e4-4c60-959e-8cb1c47cda3d"),sQuery(id+"F0.wireOp",EDGE,"fd67a80c-15d7-4a10-bc2d-74f667f92aae"),sQuery(id+"F0.wireOp",EDGE,"ce9cbc48-37c6-4742-bee7-228e45a917e3"),sQuery(id+"F0.wireOp",EDGE,"668236f6-3d49-4ccf-890f-7b693b95a113"),sQuery(id+"F0.wireOp",EDGE,"f978c870-af19-49dc-a3f6-58e714ba6b8d"),sQuery(id+"F0.wireOp",EDGE,"3c9fd5d7-5c91-4e2a-8e90-77909dfb583b"),sQuery(id+"F0.wireOp",EDGE,"3f653433-d41a-442d-9af1-f4ba11755801"),sQuery(id+"F0.wireOp",EDGE,"3e1bc7f2-4028-408e-8046-60d3c4eab3db"),sQuery(id+"F0.wireOp",EDGE,"6e5cb531-4b2f-424d-b6a2-fd274bbfcedc"),sQuery(id+"F0.wireOp",EDGE,"47450d10-22bf-4260-9408-7e53fd283f2d"),sQuery(id+"F0.wireOp",EDGE,"6d45c327-3d4d-4948-b28d-f57c85b01b79"),sQuery(id+"F0.wireOp",EDGE,"09a427cb-33ca-4fdc-b261-2336e21235b2"),sQuery(id+"F0.wireOp",EDGE,"518944ec-1655-4f40-b183-544c6dabeccc"),sQuery(id+"F0.wireOp",EDGE,"9a21c479-1b04-474c-b49a-7bb92b3e97ee"),sQuery(id+"F0.wireOp",EDGE,"96faa4f8-2343-44d0-b0c9-daf9f0cf2026"),sQuery(id+"F0.wireOp",EDGE,"6fc17f55-5333-4b57-a339-275bf10e1425"),sQuery(id+"F0.wireOp",EDGE,"42fdd7f3-cbb8-400e-a0d9-d82489298c17"),sQuery(id+"F0.wireOp",EDGE,"ff3833a1-8283-4137-914b-97420855596c"),sQuery(id+"F0.wireOp",EDGE,"6d86c47c-1e01-4b32-ae2a-396aeb5aa8c3"),sQuery(id+"F0.wireOp",EDGE,"3656029b-9af7-4a6b-91c7-0cb8f82c84b0"),sQuery(id+"F0.wireOp",EDGE,"c5a5c181-3903-47b5-9841-0451d0b8c190"),sQuery(id+"F0.wireOp",EDGE,"6b476b77-b2de-421b-b26d-88dcbb17dccc"),sQuery(id+"F0.wireOp",EDGE,"3d318069-a1b2-4ca5-910a-b32c13e6ff0f"),sQuery(id+"F0.wireOp",EDGE,"9330180f-a560-47bb-918b-d92eebda0b31"),sQuery(id+"F0.wireOp",EDGE,"b318f770-8e99-4d49-b667-ae16576ab8c5"),sQuery(id+"F0.wireOp",EDGE,"e8c7022b-339d-4a50-8e2c-c0ad6522d806"),sQuery(id+"F0.wireOp",EDGE,"e86b4955-e698-4ab7-84b9-7f9632085e45"),sQuery(id+"F0.wireOp",EDGE,"0c38cf30-4431-4dda-a171-e1c8e016ea24"),sQuery(id+"F0.wireOp",EDGE,"f094b2ba-6a66-4d13-8490-6bb0ce785aa8"),sQuery(id+"F0.wireOp",EDGE,"41e1ebd6-8c90-401f-a72a-f212800231e3"),sQuery(id+"F0.wireOp",EDGE,"40e70cb6-71ec-4d67-b914-e8ee82708b93"),sQuery(id+"F0.wireOp",EDGE,"13f06e0a-f10b-47e7-959c-6b309f65aed5"),sQuery(id+"F0.wireOp",EDGE,"3fa473f8-a0ea-440b-8ccf-443d736f73d8"),sQuery(id+"F0.wireOp",EDGE,"3ff53a63-1f71-4b9e-b5b1-fe861864c7b9"),sQuery(id+"F0.wireOp",EDGE,"9fd11a8c-801f-433b-8a68-149d040764ea"),sQuery(id+"F0.wireOp",EDGE,"2b57bb01-2787-4d2a-a1f7-a8f2ac708940"),sQuery(id+"F0.wireOp",EDGE,"b3a649f2-00b2-4941-a5f4-54f2790e47c9"),sQuery(id+"F0.wireOp",EDGE,"689af078-1fc4-4801-82f7-c259a968d8e3"),sQuery(id+"F0.wireOp",EDGE,"4afb566c-1766-4da3-aeca-2e561b661cbf"),sQuery(id+"F0.wireOp",EDGE,"afbdcd0b-9ccb-41a6-b5df-fe1bcf30544d"),sQuery(id+"F0.wireOp",EDGE,"0a1a2607-09d2-45da-b494-66f0f4572d53"),sQuery(id+"F0.wireOp",EDGE,"df9dc95f-9734-4203-a4b0-b50527c86d60"),sQuery(id+"F0.wireOp",EDGE,"868db6a5-4ab0-468d-816c-25f0bc18b053"),sQuery(id+"F0.wireOp",EDGE,"aaa1c0b5-afc6-4e25-82a0-d6f0aaf8ec45"),sQuery(id+"F0.wireOp",EDGE,"450ffb83-aa88-433e-99e9-7fc4bc443133"),sQuery(id+"F0.wireOp",EDGE,"7c9dc92b-bdbd-4c2f-ba2f-b681be311a02"),sQuery(id+"F0.wireOp",EDGE,"d8d805bb-8432-4448-99fe-12ddf517f87f"),sQuery(id+"F0.wireOp",EDGE,"e1c897c1-2833-4eab-81cd-6ccc64de02e8"),sQuery(id+"F0.wireOp",EDGE,"12eef9dd-bb38-451e-8b46-68758d02cc0e"),sQuery(id+"F0.wireOp",EDGE,"f6b90299-a189-4960-beb2-75c4f087d852"),sQuery(id+"F0.wireOp",EDGE,"d44cce74-31fd-4baf-a4a6-ccbb4521b524"),sQuery(id+"F0.wireOp",EDGE,"26311da7-8aed-42c2-aa0d-06719439663e"),sQuery(id+"F0.wireOp",EDGE,"bfe2dd46-ca33-42a6-b3e5-4bcb679aff27"),sQuery(id+"F0.wireOp",EDGE,"f7121924-5964-4ee7-8e7a-9366b6055faf"),sQuery(id+"F0.wireOp",EDGE,"baddc95a-3768-4696-a9fc-c3c93e777550"),sQuery(id+"F0.wireOp",EDGE,"4cbcd0b8-8d3f-4500-b314-949e4192bba6"),sQuery(id+"F0.wireOp",EDGE,"573feae8-dbb2-4ee3-84b1-a2f0e784b4ce"),sQuery(id+"F0.wireOp",EDGE,"1491502b-4fac-4339-bddb-72d872b244a9"),sQuery(id+"F0.wireOp",EDGE,"ed8966f0-f9a2-415f-b3ef-00e8bec5a987"),sQuery(id+"F0.wireOp",EDGE,"42659012-de86-4715-a0b8-c198bc09b6c3"),sQuery(id+"F0.wireOp",EDGE,"eba869ca-ba70-4ef3-90af-459470689084"),sQuery(id+"F0.wireOp",EDGE,"9875f08d-c713-4704-93cd-788487ec0e6b"),sQuery(id+"F0.wireOp",EDGE,"88c7c1a6-46c1-45f7-a284-4e760e0ff227"),sQuery(id+"F0.wireOp",EDGE,"7296298e-4422-4531-89ec-245f94a1b7ce"),sQuery(id+"F0.wireOp",EDGE,"d982fd75-f615-4661-88e5-4d338e35f5d6"),sQuery(id+"F0.wireOp",EDGE,"855cb7c2-4006-4b69-ae1d-061ed893761e"),sQuery(id+"F0.wireOp",EDGE,"25f14cae-63dd-43dd-a2cf-069ce091aab3"),sQuery(id+"F0.wireOp",EDGE,"8dd2c990-ce8b-4ae6-88a5-6f7d81b76fb7"),sQuery(id+"F0.wireOp",EDGE,"50c487b6-7ae5-43ad-9b89-c44e1cfbe420"),sQuery(id+"F0.wireOp",EDGE,"28defd30-3f37-4457-b5ce-98c8ab6f0938"),sQuery(id+"F0.wireOp",EDGE,"25b26be1-608d-4fca-8147-ce63c78e7ef9"),sQuery(id+"F0.wireOp",EDGE,"55286520-3f9c-4cb0-8993-b41f90c1e7b2"),sQuery(id+"F0.wireOp",EDGE,"8b04d12e-496a-4f5a-9f87-f93561172584"),sQuery(id+"F0.wireOp",EDGE,"69f61a6b-229e-4c46-8902-5dacc0b3caa7"),sQuery(id+"F0.wireOp",EDGE,"b70ecf2a-3e9d-42b0-a09c-c895f72a43f5"),sQuery(id+"F0.wireOp",EDGE,"b4318e1e-f674-42cb-b4b4-c6a7f0d1058b"),sQuery(id+"F0.wireOp",EDGE,"0a5737aa-f65d-4c08-8fa3-74cd1c6bc787"),sQuery(id+"F0.wireOp",EDGE,"2b114e95-5b76-41c0-af98-aa6b4118be67"),sQuery(id+"F0.wireOp",EDGE,"909ff558-2fcb-4b4a-b58c-44165d3143ec"),sQuery(id+"F0.wireOp",EDGE,"03647ff9-6972-4830-a77b-507609320f8a"),sQuery(id+"F0.wireOp",EDGE,"784304f5-69fc-4c5d-a15a-a01099708ad1"),sQuery(id+"F0.wireOp",EDGE,"7e862998-cb3b-43fa-98f0-afa86e38354f"),sQuery(id+"F0.wireOp",EDGE,"b133dd31-da7f-4d34-b041-a02e12d47f77"),sQuery(id+"F0.wireOp",EDGE,"c20fe978-2982-45a4-865c-b8fa9effb66d"),sQuery(id+"F0.wireOp",EDGE,"ecc07ede-e418-4cc6-ac17-b0618c730539"),sQuery(id+"F0.wireOp",EDGE,"a72532f4-d06f-446a-a491-5e0e52dccc34"),sQuery(id+"F0.wireOp",EDGE,"e80db44c-f0a2-44c0-9d9a-ac9ec1fdb025"),sQuery(id+"F0.wireOp",EDGE,"a256cc86-e2ce-4537-87d8-996e6a32e2c3"),sQuery(id+"F0.wireOp",EDGE,"9d600fab-17dd-4d7f-9bf9-2e90aad73a65"),sQuery(id+"F0.wireOp",EDGE,"5042385b-9870-4c5e-be6a-0c3db3c46120"),sQuery(id+"F0.wireOp",EDGE,"31a5a34f-51f7-4c3e-8b64-8b1dabd0146e"),sQuery(id+"F0.wireOp",EDGE,"6b2aa247-f6cb-4ed4-b715-b1f137de6caf"),sQuery(id+"F0.wireOp",EDGE,"66b72c40-0d5e-4a0b-9279-31ab5fa1e7fe"),sQuery(id+"F0.wireOp",EDGE,"15e6370f-fd6b-4262-9e07-4cd19af6e575"),sQuery(id+"F0.wireOp",EDGE,"42ae2dfc-64aa-47e2-8300-2f233e3b2cdc"),sQuery(id+"F0.wireOp",EDGE,"f1330061-7111-4682-b376-6b8410619920"),sQuery(id+"F0.wireOp",EDGE,"4f299f36-5b62-45e5-935a-49dea53b4436"),sQuery(id+"F0.wireOp",EDGE,"f4a1d07d-759c-4b8c-a361-16f86e8a581b"),sQuery(id+"F0.wireOp",EDGE,"a197af79-e1d5-4cc2-bcad-7eec1b0bb374"),sQuery(id+"F0.wireOp",EDGE,"0b645705-9a78-41e4-bf43-11811c5310d6"),sQuery(id+"F0.wireOp",EDGE,"3b8b7332-f98f-4427-9e20-b42ec5fb5940"),sQuery(id+"F0.wireOp",EDGE,"dac7c135-5026-46cf-917a-981712ef2904"),sQuery(id+"F0.wireOp",EDGE,"e792f283-39e8-4103-9782-e05d206dbdd8"),sQuery(id+"F0.wireOp",EDGE,"c4719064-44fe-4252-b3a6-de5fb7a830d2"),sQuery(id+"F0.wireOp",EDGE,"0bf6103d-bcda-4bbf-96c7-54e6ef03cde9"),sQuery(id+"F0.wireOp",EDGE,"e9d37db2-ae33-474e-9755-d6a2f55bc904"),subQ3,sQuery(id+"F0.wireOp",EDGE,"E0.left"),sQuery(id+"F0.wireOp",EDGE,"E0.right")])],"isStart":false}),makeQuery(id+"F3.opExtrude","SWEPT_FACE",FACE,{"disambiguationData":[OSD([subQ2])]})]}),makeQuery(id+"F5.opExtrude","CAP_FACE",FACE,{"disambiguationData":[OSD([subQ3,subQ2,sQuery(id+"F2.wireOp",EDGE,"E5.right"),subQ1,subQ0,sQuery(id+"F4.wireOp",EDGE,"E15.left")])],"isStart":true}),makeQuery(id+"F5.opExtrude","CAP_FACE",FACE,{"disambiguationData":[OSD([subQ3,subQ2,sQuery(id+"F2.wireOp",EDGE,"E5.left"),subQ1,subQ0,sQuery(id+"F4.wireOp",EDGE,"E15.right")])],"isStart":true})]});}
            var sketch = newSketch(context, id + "F7", { "sketchPlane" : qUnion([Q0])});
            skLineSegment(sketch, "E16", {"start": v(0.44, 124.03) * mm, "end": v(0.44, 244.03) * mm});
            skLineSegment(sketch, "E17", {"start": v(-4.56, 244.03) * mm, "end": v(-4.56, 124.03) * mm});
            skLineSegment(sketch, "E18.bottom", {"start": v(-4.56, 244.03) * mm, "end": v(0.44, 244.03) * mm, "construction": true});
            skLineSegment(sketch, "E18.left", {"start": v(-4.56, 244.03) * mm, "end": v(-4.56, 234.73) * mm, "construction": true});
            skLineSegment(sketch, "E18.right", {"start": v(0.44, 250.03) * mm, "end": v(0.44, 244.03) * mm, "construction": true});
            skLineSegment(sketch, "E19", {"start": v(-1.06, 244.03) * mm, "end": v(-0.56, 238.03) * mm});
            skPoint(sketch, "E20", {"position": v(-2.06, 238.03) * mm});
            skPoint(sketch, "E21", {"position": v(-2.06, 244.03) * mm});
            skLineSegment(sketch, "E22", {"start": v(-3.06, 244.03) * mm, "end": v(-3.56, 238.03) * mm});
            skLineSegment(sketch, "E23", {"start": v(-2.06, 244.03) * mm, "end": v(-2.06, 238.03) * mm, "construction": true});
            skLineSegment(sketch, "E24", {"start": v(-3.56, 238.03) * mm, "end": v(-0.56, 238.03) * mm});
            skLineSegment(sketch, "E25.bottom", {"start": v(-4.56, 244.03) * mm, "end": v(-3.06, 244.03) * mm});
            skLineSegment(sketch, "E25.top", {"start": v(-4.56, 250.03) * mm, "end": v(0.44, 250.03) * mm});
            skLineSegment(sketch, "E25.left", {"start": v(-4.56, 244.03) * mm, "end": v(-4.56, 250.03) * mm});
            skLineSegment(sketch, "E25.right", {"start": v(0.44, 244.03) * mm, "end": v(0.44, 250.03) * mm});
            skLineSegment(sketch, "E26", {"start": v(-4.56, 124.03) * mm, "end": v(-3.06, 124.03) * mm});
            skLineSegment(sketch, "E27", {"start": v(-3.06, 124.03) * mm, "end": v(-3.56, 118.03) * mm});
            skLineSegment(sketch, "E28", {"start": v(-3.56, 118.03) * mm, "end": v(-0.56, 118.03) * mm});
            skLineSegment(sketch, "E29", {"start": v(-0.56, 118.03) * mm, "end": v(-1.06, 124.03) * mm});
            skLineSegment(sketch, "E30", {"start": v(-1.06, 124.03) * mm, "end": v(0.44, 124.03) * mm});
            skLineSegment(sketch, "E31.trimOffspring", {"start": v(-3.06, 244.03) * mm, "end": v(-4.56, 244.03) * mm});
            skLineSegment(sketch, "E32", {"start": v(0.44, 244.03) * mm, "end": v(-1.06, 244.03) * mm});
            skSolve(sketch);
        }
        {
            var Q0;
            Q0=makeQuery(id+"F7.imprint","IMPRINT",FACE,{"disambiguationData":[TD([[makeQuery(id+"F7.imprint","IMPRINT",EDGE,{"derivedFrom":sQuery(id+"F7.wireOp",EDGE,"E16")}),1.0]])]});
            extrude(context, id + "F8", {"entities" : qUnion([Q0]), "oppositeDirection" : true, "depth" : 5 * mm});
        }
        {
            var Q0;
            Q0=makeQuery(id+"F5.opExtrude","SWEPT_FACE",FACE,{"disambiguationData":[OSD([sQuery(id+"F4.wireOp",EDGE,"E15.right")])]});
            var sketch = newSketch(context, id + "F9", { "sketchPlane" : qUnion([Q0])});
            skLineSegment(sketch, "E33.top", {"start": v(124.03, 0) * mm, "end": v(118.03, 0) * mm, "construction": true});
            skLineSegment(sketch, "E33.right", {"start": v(118.03, 5) * mm, "end": v(118.03, 0) * mm, "construction": true});
            skLineSegment(sketch, "E34", {"start": v(121.03, 0) * mm, "end": v(121.03, 5) * mm, "construction": true});
            skCircle(sketch, "E35", {"center": v(121.03, 2.5) * mm, "radius": 1 * mm});
            skSolve(sketch);
        }
        {
            var Q0;
            Q0=qSketchRegion(id+"F9",true);
            extrude(context, id + "F10", {"entities" : qUnion([Q0]), "operationType" : NewBodyOperationType.REMOVE, "oppositeDirection" : true, "depth" : 10 * mm});
        }
        {
            var Q0;
            Q0=makeQuery(id+"F8.opExtrude","SWEPT_FACE",FACE,{"disambiguationData":[OSD([sQuery(id+"F7.wireOp",EDGE,"E16")])]});
            var sketch = newSketch(context, id + "F11", { "sketchPlane" : qUnion([Q0])});
            skLineSegment(sketch, "E36.bottom", {"start": v(124.03, 5) * mm, "end": v(118.03, 5) * mm, "construction": true});
            skLineSegment(sketch, "E36.top", {"start": v(124.03, 0) * mm, "end": v(118.03, 0) * mm, "construction": true});
            skLineSegment(sketch, "E36.left", {"start": v(124.03, 5) * mm, "end": v(124.03, 0) * mm, "construction": true});
            skLineSegment(sketch, "E36.right", {"start": v(118.03, 5) * mm, "end": v(118.03, 0) * mm, "construction": true});
            skLineSegment(sketch, "E37", {"start": v(121.03, 5) * mm, "end": v(121.03, 0) * mm, "construction": true});
            skCircle(sketch, "E38", {"center": v(121.03, 2.5) * mm, "radius": 1 * mm});
            skSolve(sketch);
        }
        {
            var Q0;
            Q0=qSketchRegion(id+"F11",true);
            extrude(context, id + "F12", {"entities" : qUnion([Q0]), "operationType" : NewBodyOperationType.REMOVE, "oppositeDirection" : true, "depth" : 8 * mm, "hasSecondDirection" : true, "secondDirectionOppositeDirection" : false, "secondDirectionDepth" : 3 * mm});
        }
        {
            var Q0;
            Q0=makeQuery(id+"F7.imprint","IMPRINT",FACE,{"disambiguationData":[TD([[makeQuery(id+"F7.imprint","IMPRINT",EDGE,{"derivedFrom":sQuery(id+"F7.wireOp",EDGE,"E19")}),-1.0]])]});
            extrude(context, id + "F13", {"entities" : qUnion([Q0]), "operationType" : NewBodyOperationType.REMOVE, "oppositeDirection" : true, "depth" : 5 * mm});
        }
        {
            var Q0;
            {var subQ0=sQuery(id+"F7.wireOp",EDGE,"E19");Q0=makeQuery(id+"F7.imprint","IMPRINT",FACE,{"disambiguationData":[TD([[makeQuery(id+"F7.imprint","IMPRINT",EDGE,{"derivedFrom":subQ0}),-1.0]])]});}
            var Q1;
            Q1=makeQuery(id+"F7.imprint","IMPRINT",FACE,{"disambiguationData":[TD([[makeQuery(id+"F7.imprint","IMPRINT",EDGE,{"derivedFrom":sQuery(id+"F7.wireOp",EDGE,"E25.top")}),-1.0]])]});
            extrude(context, id + "F14", {"entities" : qUnion([Q0, Q1]), "oppositeDirection" : true, "depth" : 5 * mm});
        }
        {
            var Q0;
            Q0=makeQuery(id+"F14.opExtrude","SWEPT_FACE",FACE,{"disambiguationData":[OSD([sQuery(id+"F7.wireOp",EDGE,"E25.top")])]});
            var sketch = newSketch(context, id + "F15", { "sketchPlane" : qUnion([Q0])});
            skLineSegment(sketch, "E39", {"start": v(2.06, 5) * mm, "end": v(2.06, 0) * mm, "construction": true});
            skPoint(sketch, "E40.center.orphan", {"position": v(2.06, 2.5) * mm});
            skCircle(sketch, "E41", {"center": v(2.06, 2.5) * mm, "radius": 2.4 * mm});
            skSolve(sketch);
        }
        {
            var Q0;
            Q0=qSketchRegion(id+"F15",true);
            var Q1;
            {var subQ0=sQuery(id+"F15.wireOp",EDGE,"E40");var subQ1=sQuery(id+"F7.wireOp",EDGE,"E25.top");var subQ2=makeQuery(id+"F15.imprint","INTERSECT",VERTEX,{"derivedFrom":[makeQuery(id+"F14.opExtrude","CAP_EDGE",EDGE,{"disambiguationData":[OSD([subQ1])],"isStart":true}),subQ0]});Q1=makeQuery(id+"F15.imprint","IMPRINT",FACE,{"disambiguationData":[TD([[makeQuery(id+"F15.imprint","IMPRINT",EDGE,{"disambiguationData":[TD([[subQ2,1.0]])],"derivedFrom":subQ0}),1.0]])]});}
            extrude(context, id + "F16", {"entities" : qUnion([Q0, Q1]), "operationType" : NewBodyOperationType.ADD, "depth" : 50 * mm});
        }
        {
            var Q0;
            Q0=makeQuery(id+"F8.opExtrude","SWEPT_FACE",FACE,{"disambiguationData":[OSD([sQuery(id+"F7.wireOp",EDGE,"E16")])]});
            var sketch = newSketch(context, id + "F17", { "sketchPlane" : qUnion([Q0])});
            skLineSegment(sketch, "E42.bottom", {"start": v(244.03, 0) * mm, "end": v(238.03, 0) * mm, "construction": true});
            skLineSegment(sketch, "E42.top", {"start": v(244.03, 5) * mm, "end": v(238.03, 5) * mm, "construction": true});
            skLineSegment(sketch, "E42.left", {"start": v(244.03, 0) * mm, "end": v(244.03, 5) * mm, "construction": true});
            skLineSegment(sketch, "E42.right", {"start": v(238.03, 0) * mm, "end": v(238.03, 5) * mm, "construction": true});
            skLineSegment(sketch, "E43", {"start": v(238.03, 2.5) * mm, "end": v(244.03, 2.5) * mm, "construction": true});
            skCircle(sketch, "E44", {"center": v(241.03, 2.5) * mm, "radius": 1 * mm});
            skSolve(sketch);
        }
        {
            var Q0;
            Q0=makeQuery(id+"F17.imprint","IMPRINT",FACE,{"disambiguationData":[TD([[makeQuery(id+"F17.imprint","IMPRINT",EDGE,{"derivedFrom":sQuery(id+"F17.wireOp",EDGE,"E44")}),1.0]])]});
            extrude(context, id + "F18", {"entities" : qUnion([Q0]), "operationType" : NewBodyOperationType.REMOVE, "oppositeDirection" : true, "depth" : 5 * mm});
        }
        {
            var Q0;
            Q0=makeQuery(id+"F17.imprint","IMPRINT",FACE,{"disambiguationData":[TD([[makeQuery(id+"F17.imprint","IMPRINT",EDGE,{"derivedFrom":sQuery(id+"F17.wireOp",EDGE,"E44")}),1.0]])]});
            extrude(context, id + "F19", {"entities" : qUnion([Q0]), "operationType" : NewBodyOperationType.REMOVE, "oppositeDirection" : true, "depth" : 5 * mm});
        }
        {
            var Q0;
            Q0=makeQuery(id+"F14.opExtrude","SWEPT_FACE",FACE,{"disambiguationData":[OSD([sQuery(id+"F7.wireOp",EDGE,"E25.left")])]});
            var sketch = newSketch(context, id + "F20", { "sketchPlane" : qUnion([Q0])});
            skLineSegment(sketch, "E45.bottom", {"start": v(-250.03, 0) * mm, "end": v(-295.03, 0) * mm, "construction": true});
            skLineSegment(sketch, "E45.top", {"start": v(-250.03, 5) * mm, "end": v(-295.03, 5) * mm, "construction": true});
            skLineSegment(sketch, "E45.left", {"start": v(-250.03, 0) * mm, "end": v(-250.03, 5) * mm, "construction": true});
            skLineSegment(sketch, "E45.right", {"start": v(-295.03, 0) * mm, "end": v(-295.03, 5) * mm, "construction": true});
            skCircle(sketch, "E46", {"center": v(-295.03, 2.5) * mm, "radius": 1 * mm});
            skSolve(sketch);
        }
        {
            var Q0;
            Q0=qSketchRegion(id+"F20",true);
            extrude(context, id + "F21", {"entities" : qUnion([Q0]), "operationType" : NewBodyOperationType.REMOVE, "oppositeDirection" : true, "depth" : 5 * mm});
        }
    });
